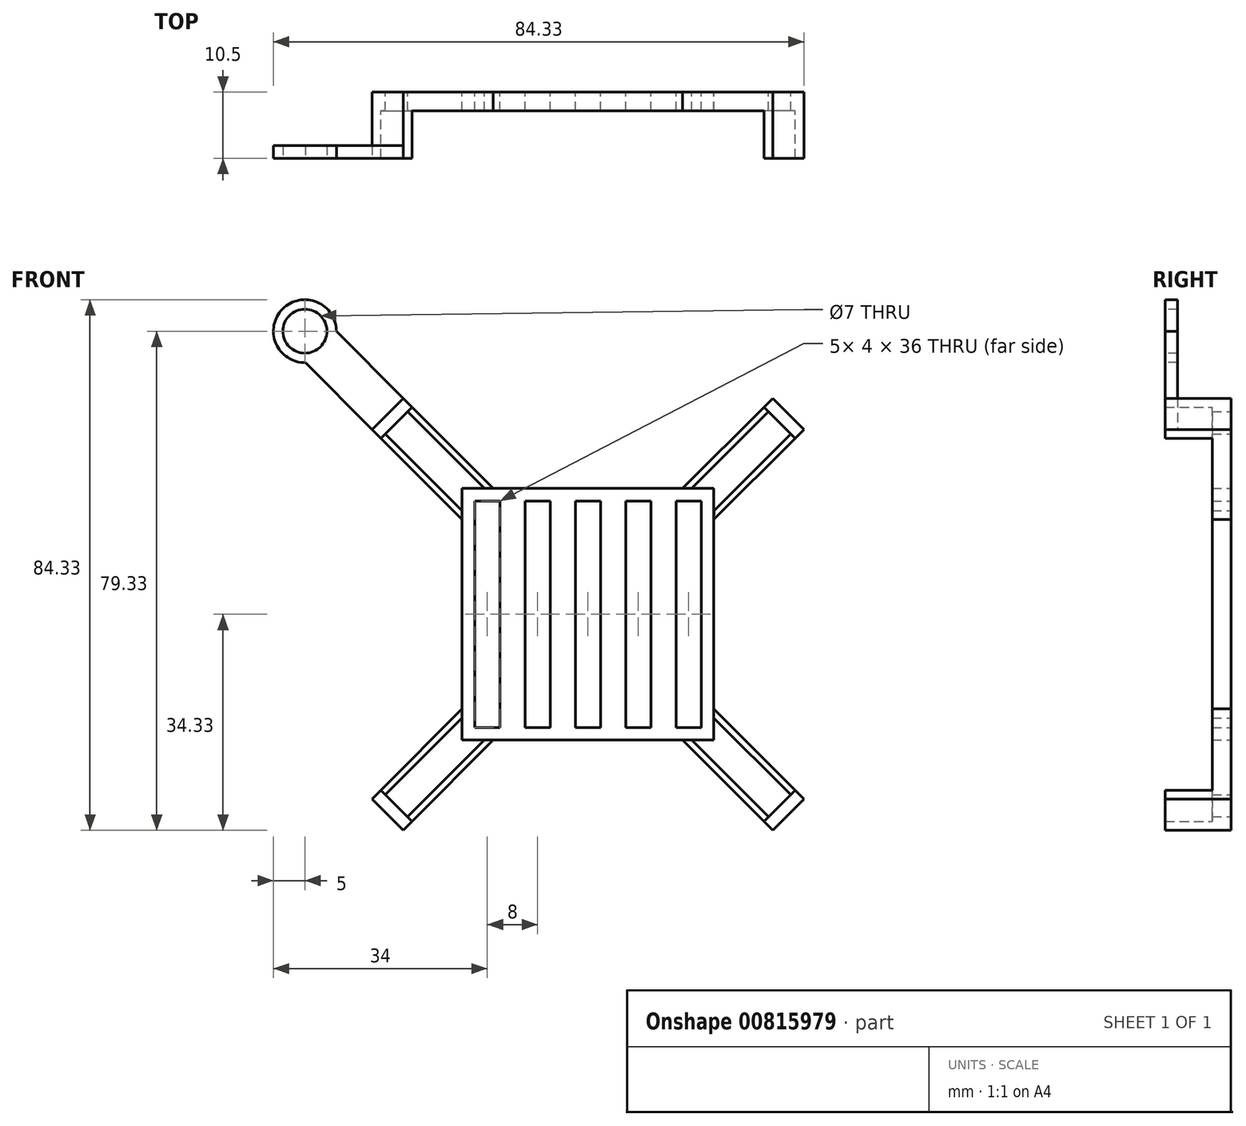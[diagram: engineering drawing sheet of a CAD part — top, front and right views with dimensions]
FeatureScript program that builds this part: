
annotation { "Feature Type Name" : "Feature", "Feature Type Description" : "" }
export const myFeature = defineFeature(function(context is Context, id is Id, definition is map)
    precondition{}
    {
        {
            var Q0;
            Q0=qCreatedBy(makeId("Front.planeOp"),FACE);
            var sketch = newSketch(context, id + "F0", { "sketchPlane" : qUnion([Q0])});
            skLineSegment(sketch, "E0.bottom", {"start": v(-20, -20) * mm, "end": v(20, -20) * mm});
            skLineSegment(sketch, "E0.top", {"start": v(-20, 20) * mm, "end": v(20, 20) * mm});
            skLineSegment(sketch, "E0.left", {"start": v(-20, -20) * mm, "end": v(-20, 20) * mm});
            skLineSegment(sketch, "E0.right", {"start": v(20, -20) * mm, "end": v(20, 20) * mm});
            skPoint(sketch, "E1", {"position": v(-18.75, 18.75) * mm});
            skPoint(sketch, "E2", {"position": v(18.75, -18.75) * mm});
            skPoint(sketch, "E3", {"position": v(-18.75, -18.75) * mm});
            skPoint(sketch, "E4", {"position": v(18.75, 18.75) * mm});
            skLineSegment(sketch, "E5.bottom", {"start": v(-18, 18) * mm, "end": v(-14, 18) * mm});
            skLineSegment(sketch, "E5.top", {"start": v(-18, -18) * mm, "end": v(-14, -18) * mm});
            skLineSegment(sketch, "E5.left", {"start": v(-18, 18) * mm, "end": v(-18, -18) * mm});
            skLineSegment(sketch, "E5.right", {"start": v(18, 18) * mm, "end": v(18, -18) * mm});
            skPoint(sketch, "E5.middle", {"position": v(0, 0) * mm});
            skLineSegment(sketch, "E6", {"start": v(-14, 18) * mm, "end": v(-14, -18) * mm});
            skLineSegment(sketch, "E7", {"start": v(-10, 18) * mm, "end": v(-10, -18) * mm});
            skLineSegment(sketch, "E8", {"start": v(-6, 18) * mm, "end": v(-6, -18) * mm});
            skLineSegment(sketch, "E9", {"start": v(14, 18) * mm, "end": v(14, -18) * mm});
            skLineSegment(sketch, "E10", {"start": v(-2, 18) * mm, "end": v(-2, -18) * mm});
            skLineSegment(sketch, "E11", {"start": v(2, 18) * mm, "end": v(2, -18) * mm});
            skLineSegment(sketch, "E12", {"start": v(6, 18) * mm, "end": v(6, -18) * mm});
            skLineSegment(sketch, "E13", {"start": v(10, 18) * mm, "end": v(10, -18) * mm});
            skLineSegment(sketch, "E14.trimOffspring", {"start": v(-10, 18) * mm, "end": v(-6, 18) * mm});
            skLineSegment(sketch, "E15.trimOffspring", {"start": v(-10, -18) * mm, "end": v(-6, -18) * mm});
            skLineSegment(sketch, "E16.trimOffspring", {"start": v(-2, 18) * mm, "end": v(2, 18) * mm});
            skLineSegment(sketch, "E17.trimOffspring", {"start": v(-2, -18) * mm, "end": v(2, -18) * mm});
            skLineSegment(sketch, "E18.trimOffspring", {"start": v(6, 18) * mm, "end": v(10, 18) * mm});
            skLineSegment(sketch, "E19.trimOffspring", {"start": v(6, -18) * mm, "end": v(10, -18) * mm});
            skLineSegment(sketch, "E20.trimOffspring", {"start": v(14, 18) * mm, "end": v(18, 18) * mm});
            skLineSegment(sketch, "E21.trimOffspring", {"start": v(14, -18) * mm, "end": v(18, -18) * mm});
            skSolve(sketch);
        }
        {
            var Q0;
            Q0 = qSketchRegion(id + "F0", true);
            extrude(context, id + "F1", {"entities" : qUnion([Q0]), "depth" : 3 * mm, "offsetDistance" : 25 * mm});
        }
        {
            var Q0;
            Q0=qCreatedBy(makeId("Front.planeOp"),FACE);
            var sketch = newSketch(context, id + "F2", { "sketchPlane" : qUnion([Q0])});
            skLineSegment(sketch, "E22", {"start": v(15.05, 20) * mm, "end": v(29.38, 34.33) * mm});
            skLineSegment(sketch, "E23", {"start": v(29.38, 34.33) * mm, "end": v(34.33, 29.38) * mm});
            skLineSegment(sketch, "E24", {"start": v(34.33, 29.38) * mm, "end": v(20, 15.05) * mm});
            skLineSegment(sketch, "E25", {"start": v(16.46, 20) * mm, "end": v(28.67, 32.2) * mm});
            skLineSegment(sketch, "E26", {"start": v(20, 16.46) * mm, "end": v(32.2, 28.67) * mm});
            skLineSegment(sketch, "E27", {"start": v(28.67, 32.2) * mm, "end": v(32.2, 28.67) * mm});
            skLineSegment(sketch, "E28.MirrorCS", {"start": v(-28.67, 32.2) * mm, "end": v(-32.2, 28.67) * mm});
            skLineSegment(sketch, "E29.MirrorCS", {"start": v(-34.33, 29.38) * mm, "end": v(-20, 15.05) * mm});
            skLineSegment(sketch, "E30.MirrorCS", {"start": v(-20, 16.46) * mm, "end": v(-32.2, 28.67) * mm});
            skLineSegment(sketch, "E31.MirrorCS", {"start": v(-16.46, 20) * mm, "end": v(-28.67, 32.2) * mm});
            skLineSegment(sketch, "E32.MirrorCS", {"start": v(-15.05, 20) * mm, "end": v(-29.38, 34.33) * mm});
            skLineSegment(sketch, "E33.MirrorCS", {"start": v(-29.38, 34.33) * mm, "end": v(-34.33, 29.38) * mm});
            skLineSegment(sketch, "E34.MirrorCS", {"start": v(-28.67, -32.2) * mm, "end": v(-32.2, -28.67) * mm});
            skLineSegment(sketch, "E35.MirrorCS", {"start": v(-20, -16.46) * mm, "end": v(-32.2, -28.67) * mm});
            skLineSegment(sketch, "E36.MirrorCS", {"start": v(-34.33, -29.38) * mm, "end": v(-20, -15.05) * mm});
            skLineSegment(sketch, "E37.MirrorCS", {"start": v(-29.38, -34.33) * mm, "end": v(-34.33, -29.38) * mm});
            skLineSegment(sketch, "E38.MirrorCS", {"start": v(-16.46, -20) * mm, "end": v(-28.67, -32.2) * mm});
            skLineSegment(sketch, "E39.MirrorCS", {"start": v(-15.05, -20) * mm, "end": v(-29.38, -34.33) * mm});
            skLineSegment(sketch, "E40.MirrorCS", {"start": v(28.67, -32.2) * mm, "end": v(32.2, -28.67) * mm});
            skLineSegment(sketch, "E41.MirrorCS", {"start": v(20, -16.46) * mm, "end": v(32.2, -28.67) * mm});
            skLineSegment(sketch, "E42.MirrorCS", {"start": v(34.33, -29.38) * mm, "end": v(20, -15.05) * mm});
            skLineSegment(sketch, "E43.MirrorCS", {"start": v(29.38, -34.33) * mm, "end": v(34.33, -29.38) * mm});
            skLineSegment(sketch, "E44.MirrorCS", {"start": v(15.05, -20) * mm, "end": v(29.38, -34.33) * mm});
            skLineSegment(sketch, "E45.MirrorCS", {"start": v(16.46, -20) * mm, "end": v(28.67, -32.2) * mm});
            skLineSegment(sketch, "E46", {"start": v(-20, 15.05) * mm, "end": v(-20, 20) * mm});
            skLineSegment(sketch, "E47", {"start": v(-15.05, 20) * mm, "end": v(-20, 20) * mm});
            skLineSegment(sketch, "E48", {"start": v(15.05, 20) * mm, "end": v(20.04, 20) * mm});
            skLineSegment(sketch, "E49", {"start": v(20.04, 20) * mm, "end": v(20, 15.05) * mm});
            skLineSegment(sketch, "E50", {"start": v(-20, -15.05) * mm, "end": v(-20, -20) * mm});
            skLineSegment(sketch, "E51", {"start": v(-15.05, -20) * mm, "end": v(-20, -20) * mm});
            skLineSegment(sketch, "E52", {"start": v(20, -15.05) * mm, "end": v(20, -20) * mm});
            skLineSegment(sketch, "E53", {"start": v(15.05, -20) * mm, "end": v(20, -20) * mm});
            skLineSegment(sketch, "E54", {"start": v(32.2, -28.67) * mm, "end": v(32.91, -27.96) * mm});
            skLineSegment(sketch, "E55", {"start": v(28.67, -32.2) * mm, "end": v(27.96, -32.91) * mm});
            skLineSegment(sketch, "E56", {"start": v(-28.67, -32.2) * mm, "end": v(-27.96, -32.91) * mm});
            skLineSegment(sketch, "E57", {"start": v(-32.2, -28.67) * mm, "end": v(-32.91, -27.96) * mm});
            skLineSegment(sketch, "E58", {"start": v(-28.67, 32.2) * mm, "end": v(-27.96, 32.91) * mm});
            skLineSegment(sketch, "E59", {"start": v(-32.2, 28.67) * mm, "end": v(-32.91, 27.96) * mm});
            skLineSegment(sketch, "E60", {"start": v(32.2, 28.67) * mm, "end": v(32.91, 27.96) * mm});
            skLineSegment(sketch, "E61", {"start": v(28.67, 32.2) * mm, "end": v(27.96, 32.91) * mm});
            skSolve(sketch);
        }
        {
            var Q0;
            Q0 = qSketchRegion(id + "F2", true);
            extrude(context, id + "F3", {"entities" : qUnion([Q0]), "depth" : 3 * mm, "offsetDistance" : 25 * mm});
        }
        {
            var Q0;
            {var subQ2=sQuery(id+"F2.wireOp",EDGE,"E25");Q0=makeQuery(id+"F2.imprint","IMPRINT",FACE,{"disambiguationData":[TD([[makeQuery(id+"F2.imprint","IMPRINT",EDGE,{"derivedFrom":subQ2}),-1.0]])]});}
            extrude(context, id + "F4", {"entities" : qUnion([Q0]), "operationType" : NewBodyOperationType.REMOVE, "depth" : 25 * mm, "offsetDistance" : 25 * mm});
        }
        {
            var Q0;
            Q0=makeQuery(id+"F2.imprint","IMPRINT",FACE,{"disambiguationData":[TD([[makeQuery(id+"F2.imprint","IMPRINT",EDGE,{"derivedFrom":sQuery(id+"F2.wireOp",EDGE,"E28.MirrorCS")}),1.0]])]});
            extrude(context, id + "F5", {"entities" : qUnion([Q0]), "operationType" : NewBodyOperationType.REMOVE, "depth" : 25 * mm, "offsetDistance" : 25 * mm});
        }
        {
            var Q0;
            Q0=makeQuery(id+"F2.imprint","IMPRINT",FACE,{"disambiguationData":[TD([[makeQuery(id+"F2.imprint","IMPRINT",EDGE,{"derivedFrom":sQuery(id+"F2.wireOp",EDGE,"E40.MirrorCS")}),1.0]])]});
            extrude(context, id + "F6", {"entities" : qUnion([Q0]), "operationType" : NewBodyOperationType.REMOVE, "depth" : 25 * mm, "offsetDistance" : 25 * mm});
        }
        {
            var Q0;
            Q0=makeQuery(id+"F2.imprint","IMPRINT",FACE,{"disambiguationData":[TD([[makeQuery(id+"F2.imprint","IMPRINT",EDGE,{"derivedFrom":sQuery(id+"F2.wireOp",EDGE,"E34.MirrorCS")}),-1.0]])]});
            extrude(context, id + "F7", {"entities" : qUnion([Q0]), "operationType" : NewBodyOperationType.REMOVE, "depth" : 25 * mm, "offsetDistance" : 25 * mm});
        }
        {
            var Q0;
            Q0=makeQuery(id+"F3.opExtrude","CAP_FACE",FACE,{"disambiguationData":[OSD([sQuery(id+"F2.wireOp",EDGE,"E42.MirrorCS"),sQuery(id+"F2.wireOp",EDGE,"E43.MirrorCS"),sQuery(id+"F2.wireOp",EDGE,"E44.MirrorCS"),sQuery(id+"F2.wireOp",EDGE,"E52"),sQuery(id+"F2.wireOp",EDGE,"E53")])],"isStart":false});
            var sketch = newSketch(context, id + "F8", { "sketchPlane" : qUnion([Q0])});
            skPoint(sketch, "E62.0", {"position": v(-30.44, -30.44) * mm});
            skLineSegment(sketch, "E63.0", {"start": v(-29.38, -34.33) * mm, "end": v(-34.33, -29.38) * mm});
            skPoint(sketch, "E64.0", {"position": v(-32.2, -28.67) * mm});
            skLineSegment(sketch, "E65.0", {"start": v(-28.67, -32.2) * mm, "end": v(-32.2, -28.67) * mm});
            skPoint(sketch, "E66.0", {"position": v(-32.91, -27.96) * mm});
            skPoint(sketch, "E67.0", {"position": v(-27.96, -32.91) * mm});
            skPoint(sketch, "E68.0", {"position": v(-28.32, -32.56) * mm});
            skLineSegment(sketch, "E69.0", {"start": v(-28.67, -32.2) * mm, "end": v(-27.96, -32.91) * mm});
            skLineSegment(sketch, "E70.0", {"start": v(-32.2, -28.67) * mm, "end": v(-32.91, -27.96) * mm});
            skLineSegment(sketch, "E71.0", {"start": v(-15.05, -20) * mm, "end": v(-29.38, -34.33) * mm});
            skLineSegment(sketch, "E72.0", {"start": v(-34.33, -29.38) * mm, "end": v(-20, -15.05) * mm});
            skLineSegment(sketch, "E73.0", {"start": v(28.67, -32.2) * mm, "end": v(32.2, -28.67) * mm});
            skLineSegment(sketch, "E74.0", {"start": v(29.38, -34.33) * mm, "end": v(34.33, -29.38) * mm});
            skPoint(sketch, "E75.0", {"position": v(32.56, -28.32) * mm});
            skPoint(sketch, "E76.0", {"position": v(32.91, -27.96) * mm});
            skLineSegment(sketch, "E77.0", {"start": v(32.2, -28.67) * mm, "end": v(32.91, -27.96) * mm});
            skLineSegment(sketch, "E78.0", {"start": v(28.67, -32.2) * mm, "end": v(27.96, -32.91) * mm});
            skLineSegment(sketch, "E79.0", {"start": v(-29.38, 34.33) * mm, "end": v(-34.33, 29.38) * mm});
            skLineSegment(sketch, "E80.0", {"start": v(-28.67, 32.2) * mm, "end": v(-32.2, 28.67) * mm});
            skLineSegment(sketch, "E81", {"start": v(27.96, -32.91) * mm, "end": v(29.38, -34.33) * mm});
            skLineSegment(sketch, "E82", {"start": v(32.91, -27.96) * mm, "end": v(34.33, -29.38) * mm});
            skLineSegment(sketch, "E83", {"start": v(-28.67, 32.2) * mm, "end": v(-27.96, 32.91) * mm});
            skLineSegment(sketch, "E84", {"start": v(-29.38, 34.33) * mm, "end": v(-27.96, 32.91) * mm});
            skLineSegment(sketch, "E85", {"start": v(-32.2, 28.67) * mm, "end": v(-32.91, 27.96) * mm});
            skLineSegment(sketch, "E86", {"start": v(-32.91, 27.96) * mm, "end": v(-34.33, 29.38) * mm});
            skLineSegment(sketch, "E87", {"start": v(32.91, -27.96) * mm, "end": v(32.2, -28.67) * mm});
            skPoint(sketch, "E88.0", {"position": v(31.85, 31.85) * mm});
            skLineSegment(sketch, "E89.0", {"start": v(29.38, 34.33) * mm, "end": v(34.33, 29.38) * mm});
            skLineSegment(sketch, "E90.0", {"start": v(28.67, 32.2) * mm, "end": v(32.2, 28.67) * mm});
            skLineSegment(sketch, "E91.0", {"start": v(28.67, 32.2) * mm, "end": v(27.96, 32.91) * mm});
            skLineSegment(sketch, "E92.0", {"start": v(32.2, 28.67) * mm, "end": v(32.91, 27.96) * mm});
            skLineSegment(sketch, "E93", {"start": v(29.38, 34.33) * mm, "end": v(27.96, 32.91) * mm});
            skLineSegment(sketch, "E94", {"start": v(34.33, 29.38) * mm, "end": v(32.91, 27.96) * mm});
            skSolve(sketch);
        }
        {
            var Q0;
            Q0 = qSketchRegion(id + "F8", true);
            extrude(context, id + "F9", {"entities" : qUnion([Q0]), "operationType" : NewBodyOperationType.ADD, "depth" : 7.5 * mm, "offsetDistance" : 25 * mm});
        }
        {
            var Q0;
            Q0=makeQuery(id+"F9.opExtrude","CAP_FACE",FACE,{"disambiguationData":[OSD([sQuery(id+"F8.wireOp",EDGE,"E79.0"),sQuery(id+"F8.wireOp",EDGE,"E80.0"),sQuery(id+"F8.wireOp",EDGE,"E83"),sQuery(id+"F8.wireOp",EDGE,"E84"),sQuery(id+"F8.wireOp",EDGE,"E85"),sQuery(id+"F8.wireOp",EDGE,"E86")])],"isStart":false});
            var sketch = newSketch(context, id + "F10", { "sketchPlane" : qUnion([Q0])});
            skLineSegment(sketch, "E95.0", {"start": v(-29.38, 34.33) * mm, "end": v(-34.33, 29.38) * mm});
            skLineSegment(sketch, "E96", {"start": v(-34.33, 29.38) * mm, "end": v(-44.95, 40) * mm});
            skCircle(sketch, "E97", {"center": v(-45, 45) * mm, "radius": 3.5 * mm});
            skArc(sketch, "E98", {"start": v(-40, 44.95) * mm, "mid": v(-48.54, 48.54) * mm, "end": v(-44.95, 40) * mm});
            skLineSegment(sketch, "E99", {"start": v(-29.38, 34.33) * mm, "end": v(-40, 44.95) * mm});
            skSolve(sketch);
        }
        {
            var Q0;
            Q0=makeQuery(id+"F10.imprint","IMPRINT",FACE,{"disambiguationData":[TD([[makeQuery(id+"F10.imprint","IMPRINT",EDGE,{"derivedFrom":sQuery(id+"F10.wireOp",EDGE,"E95.0")}),-1.0]])]});
            extrude(context, id + "F11", {"entities" : qUnion([Q0]), "oppositeDirection" : true, "depth" : 2 * mm, "offsetDistance" : 25 * mm});
        }
        {
            var Q0;
            Q0=sQuery(id+"F10.wireOp",EDGE,"E98");
            var Q1;
            Q1=sQuery(id+"F10.wireOp",EDGE,"E97");
            extrude(context, id + "F12", {"bodyType" : ToolBodyType.SURFACE, "surfaceEntities" : qUnion([Q0, Q1]), "oppositeDirection" : true, "depth" : 2.5 * mm, "offsetDistance" : 25 * mm, "hasSecondDirection" : true, "secondDirectionOppositeDirection" : false, "secondDirectionDepth" : 10.5 * mm});
        }
    });
